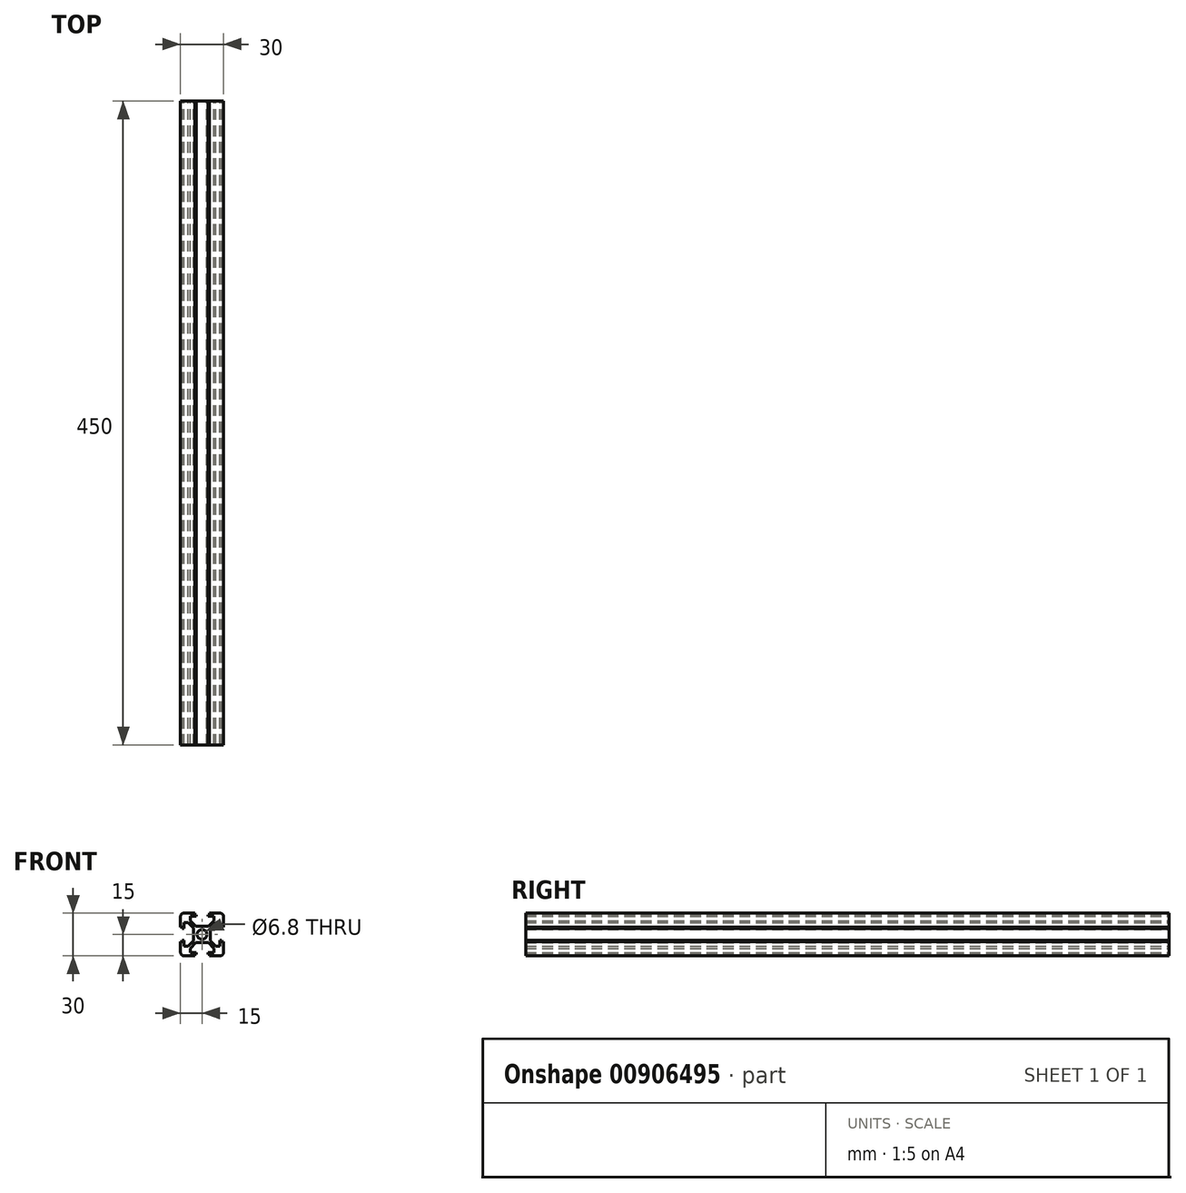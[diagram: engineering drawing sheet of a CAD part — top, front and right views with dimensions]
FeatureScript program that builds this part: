
annotation { "Feature Type Name" : "Feature", "Feature Type Description" : "" }
export const myFeature = defineFeature(function(context is Context, id is Id, definition is map)
    precondition{}
    {
        {
            var Q0;
            Q0=qCreatedBy(makeId("Front.planeOp"),FACE);
            var sketch = newSketch(context, id + "F0", { "sketchPlane" : qUnion([Q0])});
            skArc(sketch, "E0", {"start": v(0, 3.4) * mm, "mid": v(2.4, 2.4) * mm, "end": v(3.4, 0) * mm});
            skPoint(sketch, "E1", {"position": v(15, 0) * mm});
            skPoint(sketch, "E2", {"position": v(5.8, 0) * mm});
            skPoint(sketch, "E3", {"position": v(0, 15) * mm});
            skPoint(sketch, "E4", {"position": v(0, 5.8) * mm});
            skPoint(sketch, "E5", {"position": v(8.25, 8.25) * mm});
            skPoint(sketch, "E6", {"position": v(15, 5.1) * mm});
            skPoint(sketch, "E7", {"position": v(12.6, 0) * mm});
            skPoint(sketch, "E8", {"position": v(0, 12.6) * mm});
            skPoint(sketch, "E9", {"position": v(5.1, 15) * mm});
            skPoint(sketch, "E10", {"position": v(4.1, 12.6) * mm});
            skPoint(sketch, "E11", {"position": v(12.6, 4.1) * mm});
            skLineSegment(sketch, "E12", {"start": v(5.1, 15) * mm, "end": v(12.5, 15) * mm});
            skLineSegment(sketch, "E13", {"start": v(15, 12.5) * mm, "end": v(15, 5.1) * mm});
            skPoint(sketch, "E14.visualSharp", {"position": v(15, 15) * mm});
            skArc(sketch, "E14.filletArc", {"start": v(15, 12.5) * mm, "mid": v(14.27, 14.27) * mm, "end": v(12.5, 15) * mm});
            skPoint(sketch, "E15", {"position": v(8.25, 12.6) * mm});
            skPoint(sketch, "E16", {"position": v(12.6, 8.25) * mm});
            skLineSegment(sketch, "E17", {"start": v(12.6, 4.1) * mm, "end": v(12.6, 8.25) * mm});
            skLineSegment(sketch, "E18", {"start": v(4.1, 12.6) * mm, "end": v(8.25, 12.6) * mm});
            skPoint(sketch, "E19", {"position": v(5.8, 5.8) * mm});
            skLineSegment(sketch, "E20", {"start": v(0, 5.8) * mm, "end": v(4.39, 5.8) * mm});
            skLineSegment(sketch, "E21", {"start": v(5.8, 0) * mm, "end": v(5.8, 4.39) * mm});
            skLineSegment(sketch, "E22", {"start": v(5.1, 6.5) * mm, "end": v(8.25, 9.66) * mm});
            skLineSegment(sketch, "E23", {"start": v(6.5, 5.1) * mm, "end": v(9.66, 8.25) * mm});
            skLineSegment(sketch, "E24", {"start": v(6.5, 5.1) * mm, "end": v(5.8, 4.39) * mm});
            skLineSegment(sketch, "E25", {"start": v(5.1, 6.5) * mm, "end": v(4.39, 5.8) * mm});
            skLineSegment(sketch, "E26", {"start": v(12.6, 8.25) * mm, "end": v(9.66, 8.25) * mm});
            skLineSegment(sketch, "E27", {"start": v(8.25, 12.6) * mm, "end": v(8.25, 9.66) * mm});
            skPoint(sketch, "E28", {"position": v(8.25, 9.66) * mm});
            skPoint(sketch, "E29", {"position": v(9.66, 8.25) * mm});
            skPoint(sketch, "E30", {"position": v(13.8, 5.1) * mm});
            skPoint(sketch, "E31", {"position": v(13.8, 4.1) * mm});
            skLineSegment(sketch, "E32", {"start": v(12.6, 4.1) * mm, "end": v(13.8, 4.1) * mm});
            skLineSegment(sketch, "E33", {"start": v(13.8, 5.1) * mm, "end": v(13.8, 4.1) * mm});
            skLineSegment(sketch, "E34", {"start": v(13.8, 5.1) * mm, "end": v(15, 5.1) * mm});
            skPoint(sketch, "E35", {"position": v(5.1, 13.8) * mm});
            skLineSegment(sketch, "E36", {"start": v(5.1, 15) * mm, "end": v(5.1, 13.8) * mm});
            skLineSegment(sketch, "E37", {"start": v(4.1, 13.8) * mm, "end": v(4.1, 12.6) * mm});
            skLineSegment(sketch, "E38", {"start": v(4.1, 13.8) * mm, "end": v(5.1, 13.8) * mm});
            skLineSegment(sketch, "E39.1.0", {"start": v(-5.1, 6.5) * mm, "end": v(-8.25, 9.66) * mm});
            skLineSegment(sketch, "E39.1.2", {"start": v(-6.5, 5.1) * mm, "end": v(-9.66, 8.25) * mm});
            skPoint(sketch, "E39.1.3", {"position": v(-4.1, 12.6) * mm});
            skLineSegment(sketch, "E39.1.4", {"start": v(-15, 5.1) * mm, "end": v(-15, 12.5) * mm});
            skPoint(sketch, "E39.1.6", {"position": v(-15, 15) * mm});
            skPoint(sketch, "E39.1.7", {"position": v(-8.25, 8.25) * mm});
            skLineSegment(sketch, "E39.1.8", {"start": v(-5.8, 0) * mm, "end": v(-5.8, 4.39) * mm});
            skPoint(sketch, "E39.1.9", {"position": v(-8.25, 12.6) * mm});
            skLineSegment(sketch, "E39.1.10", {"start": v(-12.5, 15) * mm, "end": v(-5.1, 15) * mm});
            skPoint(sketch, "E39.1.11", {"position": v(-5.8, 0) * mm});
            skPoint(sketch, "E39.1.12", {"position": v(-12.6, 8.25) * mm});
            skLineSegment(sketch, "E39.1.13", {"start": v(0, 5.8) * mm, "end": v(-4.39, 5.8) * mm});
            skPoint(sketch, "E39.1.14", {"position": v(-12.6, 0) * mm});
            skPoint(sketch, "E39.1.15", {"position": v(-15, 5.1) * mm});
            skLineSegment(sketch, "E39.1.16", {"start": v(-12.6, 8.25) * mm, "end": v(-9.66, 8.25) * mm});
            skPoint(sketch, "E39.1.17", {"position": v(-5.8, 5.8) * mm});
            skLineSegment(sketch, "E39.1.18", {"start": v(-12.6, 4.1) * mm, "end": v(-12.6, 8.25) * mm});
            skPoint(sketch, "E39.1.19", {"position": v(-9.66, 8.25) * mm});
            skPoint(sketch, "E39.1.20", {"position": v(-5.1, 15) * mm});
            skArc(sketch, "E39.1.21", {"start": v(-3.4, 0) * mm, "mid": v(-2.4, 2.4) * mm, "end": v(0, 3.4) * mm});
            skPoint(sketch, "E39.1.22", {"position": v(-13.8, 5.1) * mm});
            skPoint(sketch, "E39.1.23", {"position": v(-12.6, 4.1) * mm});
            skPoint(sketch, "E39.1.25", {"position": v(-4.1, 13.8) * mm});
            skPoint(sketch, "E39.1.26", {"position": v(-15, 0) * mm});
            skArc(sketch, "E39.1.27", {"start": v(-12.5, 15) * mm, "mid": v(-14.27, 14.27) * mm, "end": v(-15, 12.5) * mm});
            skPoint(sketch, "E39.1.28", {"position": v(-8.25, 9.66) * mm});
            skLineSegment(sketch, "E39.1.29", {"start": v(-4.1, 12.6) * mm, "end": v(-8.25, 12.6) * mm});
            skLineSegment(sketch, "E39.1.30", {"start": v(-8.25, 12.6) * mm, "end": v(-8.25, 9.66) * mm});
            skPoint(sketch, "E39.1.31", {"position": v(-5.1, 13.8) * mm});
            skLineSegment(sketch, "E39.1.33", {"start": v(-13.8, 4.1) * mm, "end": v(-13.8, 5.1) * mm});
            skLineSegment(sketch, "E39.1.34", {"start": v(-6.5, 5.1) * mm, "end": v(-5.8, 4.39) * mm});
            skLineSegment(sketch, "E39.1.35", {"start": v(-5.1, 6.5) * mm, "end": v(-4.39, 5.8) * mm});
            skLineSegment(sketch, "E39.1.36", {"start": v(-13.8, 4.1) * mm, "end": v(-12.6, 4.1) * mm});
            skLineSegment(sketch, "E39.1.37", {"start": v(-4.1, 12.6) * mm, "end": v(-4.1, 13.8) * mm});
            skLineSegment(sketch, "E39.1.38", {"start": v(-5.1, 13.8) * mm, "end": v(-4.1, 13.8) * mm});
            skLineSegment(sketch, "E39.1.39", {"start": v(-5.1, 13.8) * mm, "end": v(-5.1, 15) * mm});
            skLineSegment(sketch, "E39.1.40", {"start": v(-15, 5.1) * mm, "end": v(-13.8, 5.1) * mm});
            skLineSegment(sketch, "E39.2.0", {"start": v(-6.5, -5.1) * mm, "end": v(-9.66, -8.25) * mm});
            skPoint(sketch, "E39.2.1", {"position": v(-5.8, 0) * mm});
            skLineSegment(sketch, "E39.2.2", {"start": v(-5.1, -6.5) * mm, "end": v(-8.25, -9.66) * mm});
            skPoint(sketch, "E39.2.3", {"position": v(-12.6, -4.1) * mm});
            skLineSegment(sketch, "E39.2.4", {"start": v(-5.1, -15) * mm, "end": v(-12.5, -15) * mm});
            skPoint(sketch, "E39.2.5", {"position": v(-12.6, 0) * mm});
            skPoint(sketch, "E39.2.6", {"position": v(-15, -15) * mm});
            skPoint(sketch, "E39.2.7", {"position": v(-8.25, -8.25) * mm});
            skLineSegment(sketch, "E39.2.8", {"start": v(0, -5.8) * mm, "end": v(-4.39, -5.8) * mm});
            skPoint(sketch, "E39.2.9", {"position": v(-12.6, -8.25) * mm});
            skLineSegment(sketch, "E39.2.10", {"start": v(-15, -12.5) * mm, "end": v(-15, -5.1) * mm});
            skPoint(sketch, "E39.2.11", {"position": v(0, -5.8) * mm});
            skPoint(sketch, "E39.2.12", {"position": v(-8.25, -12.6) * mm});
            skLineSegment(sketch, "E39.2.13", {"start": v(-5.8, 0) * mm, "end": v(-5.8, -4.39) * mm});
            skPoint(sketch, "E39.2.14", {"position": v(0, -12.6) * mm});
            skPoint(sketch, "E39.2.15", {"position": v(-5.1, -15) * mm});
            skLineSegment(sketch, "E39.2.16", {"start": v(-8.25, -12.6) * mm, "end": v(-8.25, -9.66) * mm});
            skPoint(sketch, "E39.2.17", {"position": v(-5.8, -5.8) * mm});
            skLineSegment(sketch, "E39.2.18", {"start": v(-4.1, -12.6) * mm, "end": v(-8.25, -12.6) * mm});
            skPoint(sketch, "E39.2.19", {"position": v(-8.25, -9.66) * mm});
            skPoint(sketch, "E39.2.20", {"position": v(-15, -5.1) * mm});
            skArc(sketch, "E39.2.21", {"start": v(0, -3.4) * mm, "mid": v(-2.4, -2.4) * mm, "end": v(-3.4, 0) * mm});
            skPoint(sketch, "E39.2.22", {"position": v(-5.1, -13.8) * mm});
            skPoint(sketch, "E39.2.23", {"position": v(-4.1, -12.6) * mm});
            skPoint(sketch, "E39.2.24", {"position": v(-15, 0) * mm});
            skPoint(sketch, "E39.2.25", {"position": v(-13.8, -4.1) * mm});
            skPoint(sketch, "E39.2.26", {"position": v(0, -15) * mm});
            skArc(sketch, "E39.2.27", {"start": v(-15, -12.5) * mm, "mid": v(-14.27, -14.27) * mm, "end": v(-12.5, -15) * mm});
            skPoint(sketch, "E39.2.28", {"position": v(-9.66, -8.25) * mm});
            skLineSegment(sketch, "E39.2.29", {"start": v(-12.6, -4.1) * mm, "end": v(-12.6, -8.25) * mm});
            skLineSegment(sketch, "E39.2.30", {"start": v(-12.6, -8.25) * mm, "end": v(-9.66, -8.25) * mm});
            skPoint(sketch, "E39.2.31", {"position": v(-13.8, -5.1) * mm});
            skLineSegment(sketch, "E39.2.33", {"start": v(-4.1, -13.8) * mm, "end": v(-5.1, -13.8) * mm});
            skLineSegment(sketch, "E39.2.34", {"start": v(-5.1, -6.5) * mm, "end": v(-4.39, -5.8) * mm});
            skLineSegment(sketch, "E39.2.35", {"start": v(-6.5, -5.1) * mm, "end": v(-5.8, -4.39) * mm});
            skLineSegment(sketch, "E39.2.36", {"start": v(-4.1, -13.8) * mm, "end": v(-4.1, -12.6) * mm});
            skLineSegment(sketch, "E39.2.37", {"start": v(-12.6, -4.1) * mm, "end": v(-13.8, -4.1) * mm});
            skLineSegment(sketch, "E39.2.38", {"start": v(-13.8, -5.1) * mm, "end": v(-13.8, -4.1) * mm});
            skLineSegment(sketch, "E39.2.39", {"start": v(-13.8, -5.1) * mm, "end": v(-15, -5.1) * mm});
            skLineSegment(sketch, "E39.2.40", {"start": v(-5.1, -15) * mm, "end": v(-5.1, -13.8) * mm});
            skLineSegment(sketch, "E39.3.0", {"start": v(5.1, -6.5) * mm, "end": v(8.25, -9.66) * mm});
            skPoint(sketch, "E39.3.1", {"position": v(0, -5.8) * mm});
            skLineSegment(sketch, "E39.3.2", {"start": v(6.5, -5.1) * mm, "end": v(9.66, -8.25) * mm});
            skPoint(sketch, "E39.3.3", {"position": v(4.1, -12.6) * mm});
            skLineSegment(sketch, "E39.3.4", {"start": v(15, -5.1) * mm, "end": v(15, -12.5) * mm});
            skPoint(sketch, "E39.3.5", {"position": v(0, -12.6) * mm});
            skPoint(sketch, "E39.3.6", {"position": v(15, -15) * mm});
            skPoint(sketch, "E39.3.7", {"position": v(8.25, -8.25) * mm});
            skLineSegment(sketch, "E39.3.8", {"start": v(5.8, 0) * mm, "end": v(5.8, -4.39) * mm});
            skPoint(sketch, "E39.3.9", {"position": v(8.25, -12.6) * mm});
            skLineSegment(sketch, "E39.3.10", {"start": v(12.5, -15) * mm, "end": v(5.1, -15) * mm});
            skPoint(sketch, "E39.3.12", {"position": v(12.6, -8.25) * mm});
            skLineSegment(sketch, "E39.3.13", {"start": v(0, -5.8) * mm, "end": v(4.39, -5.8) * mm});
            skPoint(sketch, "E39.3.15", {"position": v(15, -5.1) * mm});
            skLineSegment(sketch, "E39.3.16", {"start": v(12.6, -8.25) * mm, "end": v(9.66, -8.25) * mm});
            skPoint(sketch, "E39.3.17", {"position": v(5.8, -5.8) * mm});
            skLineSegment(sketch, "E39.3.18", {"start": v(12.6, -4.1) * mm, "end": v(12.6, -8.25) * mm});
            skPoint(sketch, "E39.3.19", {"position": v(9.66, -8.25) * mm});
            skPoint(sketch, "E39.3.20", {"position": v(5.1, -15) * mm});
            skArc(sketch, "E39.3.21", {"start": v(3.4, 0) * mm, "mid": v(2.4, -2.4) * mm, "end": v(0, -3.4) * mm});
            skPoint(sketch, "E39.3.22", {"position": v(13.8, -5.1) * mm});
            skPoint(sketch, "E39.3.23", {"position": v(12.6, -4.1) * mm});
            skPoint(sketch, "E39.3.24", {"position": v(0, -15) * mm});
            skPoint(sketch, "E39.3.25", {"position": v(4.1, -13.8) * mm});
            skArc(sketch, "E39.3.27", {"start": v(12.5, -15) * mm, "mid": v(14.27, -14.27) * mm, "end": v(15, -12.5) * mm});
            skPoint(sketch, "E39.3.28", {"position": v(8.25, -9.66) * mm});
            skLineSegment(sketch, "E39.3.29", {"start": v(4.1, -12.6) * mm, "end": v(8.25, -12.6) * mm});
            skLineSegment(sketch, "E39.3.30", {"start": v(8.25, -12.6) * mm, "end": v(8.25, -9.66) * mm});
            skPoint(sketch, "E39.3.31", {"position": v(5.1, -13.8) * mm});
            skLineSegment(sketch, "E39.3.33", {"start": v(13.8, -4.1) * mm, "end": v(13.8, -5.1) * mm});
            skLineSegment(sketch, "E39.3.34", {"start": v(6.5, -5.1) * mm, "end": v(5.8, -4.39) * mm});
            skLineSegment(sketch, "E39.3.35", {"start": v(5.1, -6.5) * mm, "end": v(4.39, -5.8) * mm});
            skLineSegment(sketch, "E39.3.36", {"start": v(13.8, -4.1) * mm, "end": v(12.6, -4.1) * mm});
            skLineSegment(sketch, "E39.3.37", {"start": v(4.1, -12.6) * mm, "end": v(4.1, -13.8) * mm});
            skLineSegment(sketch, "E39.3.38", {"start": v(5.1, -13.8) * mm, "end": v(4.1, -13.8) * mm});
            skLineSegment(sketch, "E39.3.39", {"start": v(5.1, -13.8) * mm, "end": v(5.1, -15) * mm});
            skLineSegment(sketch, "E39.3.40", {"start": v(15, -5.1) * mm, "end": v(13.8, -5.1) * mm});
            skSolve(sketch);
        }
        {
            var Q0;
            Q0=qSketchRegion(id+"F0",true);
            extrude(context, id + "F1", {"entities" : qUnion([Q0]), "depth" : 450 * mm, "offsetDistance" : 25 * mm});
        }
    });
